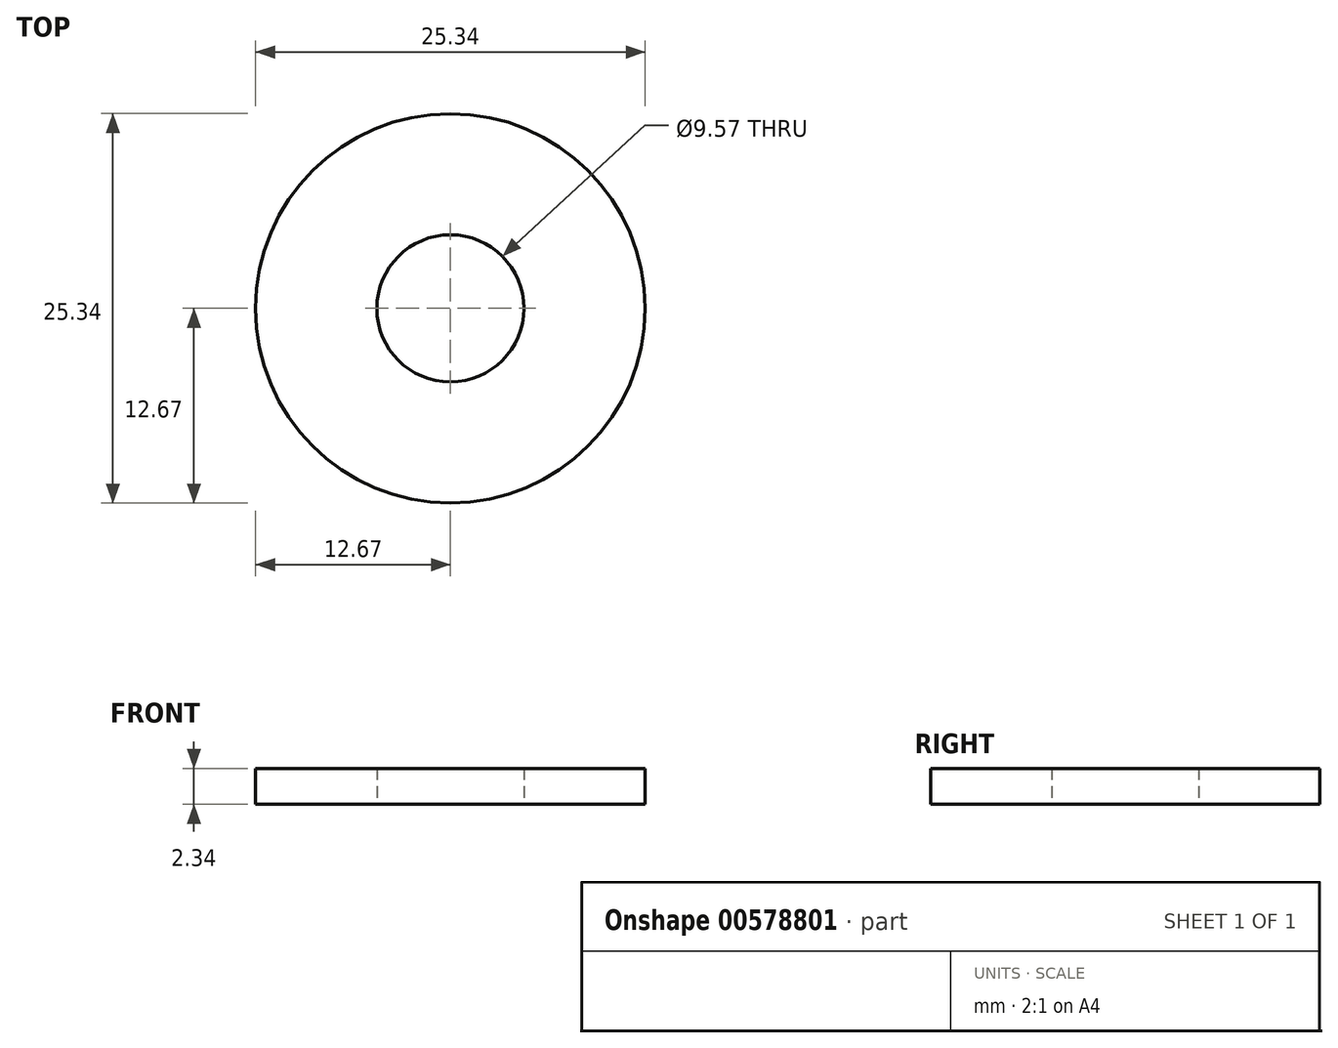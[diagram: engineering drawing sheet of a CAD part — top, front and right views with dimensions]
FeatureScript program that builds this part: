
annotation { "Feature Type Name" : "Feature", "Feature Type Description" : "" }
export const myFeature = defineFeature(function(context is Context, id is Id, definition is map)
    precondition{}
    {
        {
            var Q0;
            Q0=qCreatedBy(makeId("Top.planeOp"),FACE);
            var sketch = newSketch(context, id + "F0", { "sketchPlane" : qUnion([Q0])});
            skCircle(sketch, "E0", {"center": v(0, 0) * mm, "radius": 4.79 * mm});
            skCircle(sketch, "E1", {"center": v(0, 0) * mm, "radius": 12.66 * mm});
            skSolve(sketch);
        }
        {
            var Q0;
            Q0=makeQuery(id+"F0.imprint","IMPRINT",FACE,{"disambiguationData":[TD([[makeQuery(id+"F0.imprint","IMPRINT",EDGE,{"derivedFrom":sQuery(id+"F0.wireOp",EDGE,"E0")}),-1.0]])]});
            extrude(context, id + "F1", {"entities" : qUnion([Q0]), "depth" : 2.34 * mm, "offsetDistance" : 25 * mm});
        }
    });
